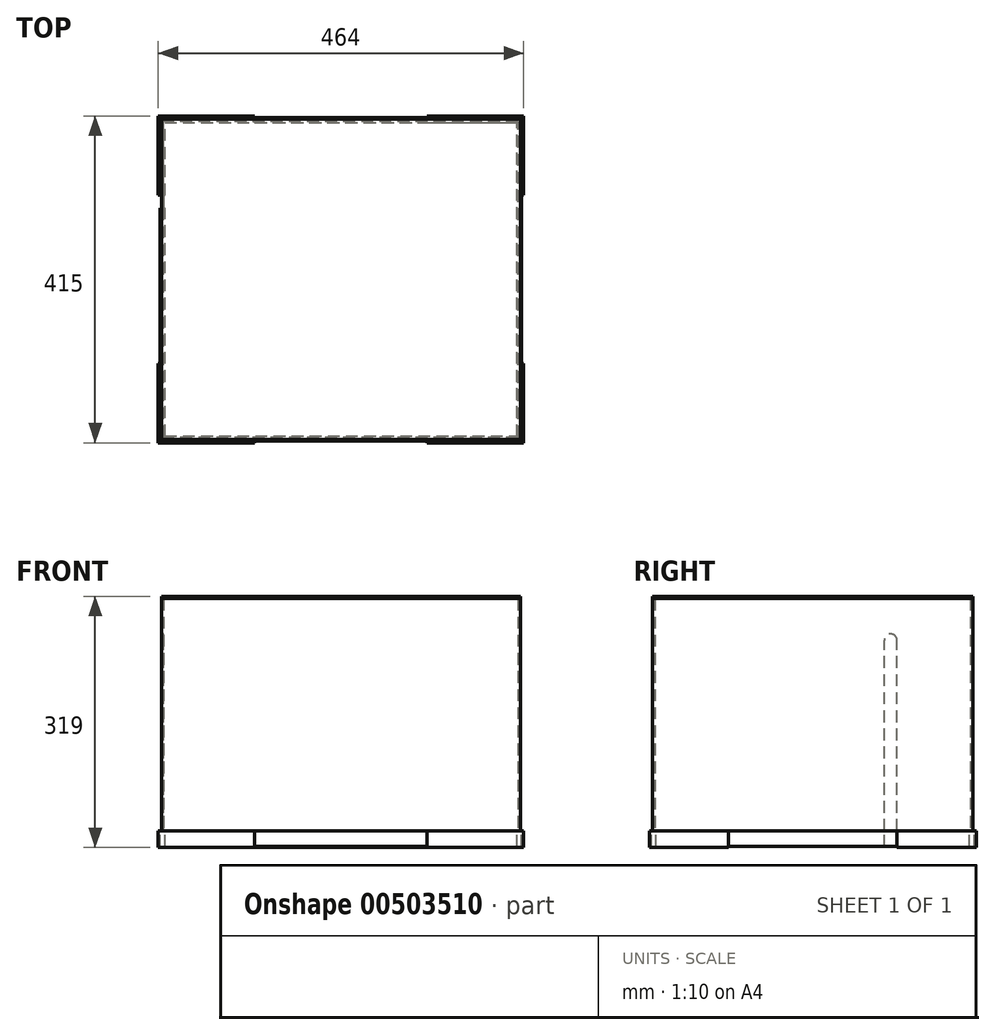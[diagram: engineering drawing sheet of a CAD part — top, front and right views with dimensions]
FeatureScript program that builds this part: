
annotation { "Feature Type Name" : "Feature", "Feature Type Description" : "" }
export const myFeature = defineFeature(function(context is Context, id is Id, definition is map)
    precondition{}
    {
        {
            var Q0;
            Q0=qCreatedBy(makeId("Right.planeOp"),FACE);
            var sketch = newSketch(context, id + "F0", { "sketchPlane" : qUnion([Q0])});
            skLineSegment(sketch, "E0.bottom", {"start": v(0, 308) * mm, "end": v(407, 308) * mm});
            skLineSegment(sketch, "E0.top", {"start": v(0, 0) * mm, "end": v(407, 0) * mm});
            skLineSegment(sketch, "E0.left", {"start": v(0, 308) * mm, "end": v(0, 0) * mm});
            skLineSegment(sketch, "E0.right", {"start": v(407, 308) * mm, "end": v(407, 0) * mm});
            skLineSegment(sketch, "E1.0", {"start": v(3, 305) * mm, "end": v(3, 0) * mm});
            skLineSegment(sketch, "E1.1", {"start": v(3, 305) * mm, "end": v(404, 305) * mm});
            skLineSegment(sketch, "E1.2", {"start": v(404, 305) * mm, "end": v(404, 0) * mm});
            skLineSegment(sketch, "E2", {"start": v(404, 305) * mm, "end": v(407, 305) * mm});
            skLineSegment(sketch, "E3", {"start": v(3, 305) * mm, "end": v(0, 305) * mm});
            skLineSegment(sketch, "E4", {"start": v(294.34, 0) * mm, "end": v(294.34, 252.03) * mm});
            skCircle(sketch, "E5", {"center": v(302.45, 252.03) * mm, "radius": 8.1 * mm});
            skLineSegment(sketch, "E6", {"start": v(310.56, 0) * mm, "end": v(310.56, 252.03) * mm});
            skSolve(sketch);
        }
        {
            var Q0;
            {var subQ0=sQuery(id+"F0.wireOp",EDGE,"E1.0");Q0=makeQuery(id+"F0.imprint","IMPRINT",FACE,{"disambiguationData":[TD([[makeQuery(id+"F0.imprint","IMPRINT",EDGE,{"derivedFrom":subQ0}),1.0]])]});}
            extrude(context, id + "F1", {"entities" : qUnion([Q0]), "depth" : 3 * mm});
        }
        {
            var Q0;
            {var subQ1=sQuery(id+"F0.wireOp",EDGE,"E0.bottom");Q0=makeQuery(id+"F0.imprint","IMPRINT",FACE,{"disambiguationData":[TD([[makeQuery(id+"F0.imprint","IMPRINT",EDGE,{"derivedFrom":subQ1}),-1.0]])]});}
            extrude(context, id + "F2", {"entities" : qUnion([Q0]), "depth" : 456 * mm});
        }
        {
            var Q0;
            {var subQ3=sQuery(id+"F0.wireOp",EDGE,"E1.0");Q0=makeQuery(id+"F0.imprint","IMPRINT",FACE,{"disambiguationData":[TD([[makeQuery(id+"F0.imprint","IMPRINT",EDGE,{"derivedFrom":subQ3}),-1.0]])]});}
            var Q1;
            {var subQ3=sQuery(id+"F0.wireOp",EDGE,"E1.2");Q1=makeQuery(id+"F0.imprint","IMPRINT",FACE,{"disambiguationData":[TD([[makeQuery(id+"F0.imprint","IMPRINT",EDGE,{"derivedFrom":subQ3}),1.0]])]});}
            extrude(context, id + "F3", {"entities" : qUnion([Q0, Q1]), "depth" : 456 * mm});
        }
        {
            var Q0;
            Q0=makeQuery(id+"F3.opExtrude","CAP_FACE",FACE,{"disambiguationData":[OSD([sQuery(id+"F0.wireOp",EDGE,"E0.top"),sQuery(id+"F0.wireOp",EDGE,"E0.left"),sQuery(id+"F0.wireOp",EDGE,"E1.0"),sQuery(id+"F0.wireOp",EDGE,"E3")])],"isStart":false});
            var sketch = newSketch(context, id + "F4", { "sketchPlane" : qUnion([Q0])});
            skLineSegment(sketch, "E7.bottom", {"start": v(3, 0) * mm, "end": v(404, 0) * mm});
            skLineSegment(sketch, "E7.top", {"start": v(3, 305) * mm, "end": v(404, 305) * mm});
            skLineSegment(sketch, "E7.left", {"start": v(3, 0) * mm, "end": v(3, 305) * mm});
            skLineSegment(sketch, "E7.right", {"start": v(404, 0) * mm, "end": v(404, 305) * mm});
            skSolve(sketch);
        }
        {
            var Q0;
            Q0=makeQuery(id+"F4.imprint","IMPRINT",FACE,{"disambiguationData":[TD([[makeQuery(id+"F4.imprint","IMPRINT",EDGE,{"derivedFrom":sQuery(id+"F4.wireOp",EDGE,"E7.bottom")}),1.0]])]});
            extrude(context, id + "F5", {"entities" : qUnion([Q0]), "oppositeDirection" : true, "depth" : 3 * mm});
        }
        {
            var Q0;
            {var subQ0=sQuery(id+"F0.wireOp",EDGE,"E0.top");Q0=makeQuery(id+"F3.opExtrude","SWEPT_FACE",FACE,{"disambiguationData":[OSD([subQ0]),TDD([makeQuery(id+"F0.imprint","IMPRINT",EDGE,{"disambiguationData":[TD([[makeQuery(id+"F0.imprint","INTERSECT",VERTEX,{"derivedFrom":[subQ0,sQuery(id+"F0.wireOp",EDGE,"E0.left")]}),-1.0]])],"derivedFrom":subQ0})])]});}
            var sketch = newSketch(context, id + "F6", { "sketchPlane" : qUnion([Q0])});
            skLineSegment(sketch, "E8.bottom", {"start": v(0, 0) * mm, "end": v(456, 0) * mm});
            skLineSegment(sketch, "E8.top", {"start": v(0, -407) * mm, "end": v(456, -407) * mm});
            skLineSegment(sketch, "E8.left", {"start": v(0, 0) * mm, "end": v(0, -407) * mm});
            skLineSegment(sketch, "E8.right", {"start": v(456, 0) * mm, "end": v(456, -407) * mm});
            skLineSegment(sketch, "E9.0", {"start": v(457.5, 1.5) * mm, "end": v(457.5, -408.5) * mm});
            skLineSegment(sketch, "E9.1", {"start": v(-1.5, 1.5) * mm, "end": v(457.5, 1.5) * mm});
            skLineSegment(sketch, "E9.2", {"start": v(-1.5, 1.5) * mm, "end": v(-1.5, -408.5) * mm});
            skLineSegment(sketch, "E9.3", {"start": v(-1.5, -408.5) * mm, "end": v(457.5, -408.5) * mm});
            skLineSegment(sketch, "E10.0", {"start": v(4.5, -4.5) * mm, "end": v(451.5, -4.5) * mm});
            skLineSegment(sketch, "E10.1", {"start": v(4.5, -4.5) * mm, "end": v(4.5, -402.5) * mm});
            skLineSegment(sketch, "E10.2", {"start": v(4.5, -402.5) * mm, "end": v(451.5, -402.5) * mm});
            skLineSegment(sketch, "E10.3", {"start": v(451.5, -4.5) * mm, "end": v(451.5, -402.5) * mm});
            skLineSegment(sketch, "E11.bottom", {"start": v(3, -3) * mm, "end": v(453, -3) * mm});
            skLineSegment(sketch, "E11.top", {"start": v(3, -404) * mm, "end": v(453, -404) * mm});
            skLineSegment(sketch, "E11.left", {"start": v(3, -3) * mm, "end": v(3, -404) * mm});
            skLineSegment(sketch, "E11.right", {"start": v(453, -3) * mm, "end": v(453, -404) * mm});
            skLineSegment(sketch, "E12", {"start": v(118.5, -408.5) * mm, "end": v(118.5, 1.5) * mm});
            skLineSegment(sketch, "E13", {"start": v(-1.5, -310.56) * mm, "end": v(457.5, -310.56) * mm});
            skLineSegment(sketch, "E14", {"start": v(337.5, -408.5) * mm, "end": v(337.5, 1.5) * mm});
            skLineSegment(sketch, "E15", {"start": v(-1.5, -96.44) * mm, "end": v(457.5, -96.44) * mm});
            skLineSegment(sketch, "E16", {"start": v(118.5, -408.5) * mm, "end": v(118.5, -310.56) * mm, "construction": true});
            skLineSegment(sketch, "E17", {"start": v(118.5, 1.5) * mm, "end": v(118.5, -96.44) * mm, "construction": true});
            skLineSegment(sketch, "E18", {"start": v(228, 1.5) * mm, "end": v(228, -408.5) * mm});
            skLineSegment(sketch, "E19", {"start": v(-1.5, -203.5) * mm, "end": v(457.5, -203.5) * mm});
            skLineSegment(sketch, "E20", {"start": v(-1.5, -294.34) * mm, "end": v(4.5, -294.34) * mm});
            skSolve(sketch);
        }
        {
            var Q0;
            {var subQ0=sQuery(id+"F6.wireOp",EDGE,"E8.left");var subQ1=sQuery(id+"F6.wireOp",EDGE,"E8.bottom");var subQ2=makeQuery(id+"F6.imprint","INTERSECT",VERTEX,{"derivedFrom":[subQ1,subQ0]});Q0=makeQuery(id+"F6.imprint","IMPRINT",FACE,{"disambiguationData":[TD([[makeQuery(id+"F6.imprint","IMPRINT",EDGE,{"disambiguationData":[TD([[subQ2,1.0]])],"derivedFrom":subQ1}),-1.0]])]});}
            var Q1;
            {var subQ5=sQuery(id+"F6.wireOp",EDGE,"E8.bottom");var subQ7=sQuery(id+"F6.wireOp",EDGE,"E8.left");var subQ9=makeQuery(id+"F6.imprint","INTERSECT",VERTEX,{"derivedFrom":[subQ5,subQ7]});Q1=makeQuery(id+"F6.imprint","IMPRINT",FACE,{"disambiguationData":[TD([[makeQuery(id+"F6.imprint","IMPRINT",EDGE,{"disambiguationData":[TD([[subQ9,1.0]])],"derivedFrom":subQ5}),1.0]])]});}
            var Q2;
            {var subQ0=sQuery(id+"F6.wireOp",EDGE,"E10.1");var subQ1=sQuery(id+"F6.wireOp",EDGE,"E10.0");var subQ2=makeQuery(id+"F6.imprint","INTERSECT",VERTEX,{"derivedFrom":[subQ1,subQ0]});Q2=makeQuery(id+"F6.imprint","IMPRINT",FACE,{"disambiguationData":[TD([[makeQuery(id+"F6.imprint","IMPRINT",EDGE,{"disambiguationData":[TD([[subQ2,-1.0]])],"derivedFrom":subQ1}),1.0]])]});}
            var Q3;
            {var subQ0=sQuery(id+"F6.wireOp",EDGE,"E8.left");var subQ3=sQuery(id+"F6.wireOp",EDGE,"E15");var subQ4=makeQuery(id+"F6.imprint","INTERSECT",VERTEX,{"derivedFrom":[subQ0,subQ3]});Q3=makeQuery(id+"F6.imprint","IMPRINT",FACE,{"disambiguationData":[TD([[makeQuery(id+"F6.imprint","IMPRINT",EDGE,{"disambiguationData":[TD([[subQ4,-1.0]])],"derivedFrom":subQ3}),1.0]])]});}
            var Q4;
            {var subQ7=sQuery(id+"F6.wireOp",EDGE,"E8.left");var subQ8=sQuery(id+"F6.wireOp",EDGE,"E8.top");var subQ9=makeQuery(id+"F6.imprint","INTERSECT",VERTEX,{"derivedFrom":[subQ8,subQ7]});Q4=makeQuery(id+"F6.imprint","IMPRINT",FACE,{"disambiguationData":[TD([[makeQuery(id+"F6.imprint","IMPRINT",EDGE,{"disambiguationData":[TD([[subQ9,-1.0]])],"derivedFrom":subQ8}),-1.0]])]});}
            var Q5;
            {var subQ7=sQuery(id+"F6.wireOp",EDGE,"E8.left");var subQ8=sQuery(id+"F6.wireOp",EDGE,"E8.top");var subQ9=makeQuery(id+"F6.imprint","INTERSECT",VERTEX,{"derivedFrom":[subQ8,subQ7]});Q5=makeQuery(id+"F6.imprint","IMPRINT",FACE,{"disambiguationData":[TD([[makeQuery(id+"F6.imprint","IMPRINT",EDGE,{"disambiguationData":[TD([[subQ9,-1.0]])],"derivedFrom":subQ8}),1.0]])]});}
            var Q6;
            {var subQ7=sQuery(id+"F6.wireOp",EDGE,"E10.2");var subQ8=sQuery(id+"F6.wireOp",EDGE,"E10.1");var subQ9=makeQuery(id+"F6.imprint","INTERSECT",VERTEX,{"derivedFrom":[subQ8,subQ7]});Q6=makeQuery(id+"F6.imprint","IMPRINT",FACE,{"disambiguationData":[TD([[makeQuery(id+"F6.imprint","IMPRINT",EDGE,{"disambiguationData":[TD([[subQ9,1.0]])],"derivedFrom":subQ8}),-1.0]])]});}
            var Q7;
            {var subQ5=sQuery(id+"F6.wireOp",EDGE,"E8.top");var subQ7=sQuery(id+"F6.wireOp",EDGE,"E8.right");var subQ8=makeQuery(id+"F6.imprint","INTERSECT",VERTEX,{"derivedFrom":[subQ5,subQ7]});Q7=makeQuery(id+"F6.imprint","IMPRINT",FACE,{"disambiguationData":[TD([[makeQuery(id+"F6.imprint","IMPRINT",EDGE,{"disambiguationData":[TD([[subQ8,1.0]])],"derivedFrom":subQ5}),-1.0]])]});}
            var Q8;
            {var subQ6=sQuery(id+"F6.wireOp",EDGE,"E8.top");var subQ9=sQuery(id+"F6.wireOp",EDGE,"E8.right");var subQ10=makeQuery(id+"F6.imprint","INTERSECT",VERTEX,{"derivedFrom":[subQ6,subQ9]});Q8=makeQuery(id+"F6.imprint","IMPRINT",FACE,{"disambiguationData":[TD([[makeQuery(id+"F6.imprint","IMPRINT",EDGE,{"disambiguationData":[TD([[subQ10,1.0]])],"derivedFrom":subQ6}),1.0]])]});}
            var Q9;
            {var subQ7=sQuery(id+"F6.wireOp",EDGE,"E10.3");var subQ8=sQuery(id+"F6.wireOp",EDGE,"E10.2");var subQ9=makeQuery(id+"F6.imprint","INTERSECT",VERTEX,{"derivedFrom":[subQ8,subQ7]});Q9=makeQuery(id+"F6.imprint","IMPRINT",FACE,{"disambiguationData":[TD([[makeQuery(id+"F6.imprint","IMPRINT",EDGE,{"disambiguationData":[TD([[subQ9,1.0]])],"derivedFrom":subQ8}),-1.0]])]});}
            var Q10;
            {var subQ5=sQuery(id+"F6.wireOp",EDGE,"E8.right");var subQ8=sQuery(id+"F6.wireOp",EDGE,"E8.bottom");var subQ9=makeQuery(id+"F6.imprint","INTERSECT",VERTEX,{"derivedFrom":[subQ8,subQ5]});Q10=makeQuery(id+"F6.imprint","IMPRINT",FACE,{"disambiguationData":[TD([[makeQuery(id+"F6.imprint","IMPRINT",EDGE,{"disambiguationData":[TD([[subQ9,-1.0]])],"derivedFrom":subQ8}),-1.0]])]});}
            var Q11;
            {var subQ1=sQuery(id+"F6.wireOp",EDGE,"E8.bottom");var subQ7=sQuery(id+"F6.wireOp",EDGE,"E8.right");var subQ8=makeQuery(id+"F6.imprint","INTERSECT",VERTEX,{"derivedFrom":[subQ1,subQ7]});Q11=makeQuery(id+"F6.imprint","IMPRINT",FACE,{"disambiguationData":[TD([[makeQuery(id+"F6.imprint","IMPRINT",EDGE,{"disambiguationData":[TD([[subQ8,-1.0]])],"derivedFrom":subQ1}),1.0]])]});}
            var Q12;
            {var subQ7=sQuery(id+"F6.wireOp",EDGE,"E10.0");var subQ9=sQuery(id+"F6.wireOp",EDGE,"E10.3");var subQ10=makeQuery(id+"F6.imprint","INTERSECT",VERTEX,{"derivedFrom":[subQ7,subQ9]});Q12=makeQuery(id+"F6.imprint","IMPRINT",FACE,{"disambiguationData":[TD([[makeQuery(id+"F6.imprint","IMPRINT",EDGE,{"disambiguationData":[TD([[subQ10,1.0]])],"derivedFrom":subQ7}),1.0]])]});}
            var Q13;
            {var subQ0=sQuery(id+"F6.wireOp",EDGE,"E8.right");var subQ3=sQuery(id+"F6.wireOp",EDGE,"E15");var subQ4=makeQuery(id+"F6.imprint","INTERSECT",VERTEX,{"derivedFrom":[subQ0,subQ3]});Q13=makeQuery(id+"F6.imprint","IMPRINT",FACE,{"disambiguationData":[TD([[makeQuery(id+"F6.imprint","IMPRINT",EDGE,{"disambiguationData":[TD([[subQ4,1.0]])],"derivedFrom":subQ3}),1.0]])]});}
            extrude(context, id + "F7", {"entities" : qUnion([Q0, Q1, Q2, Q3, Q4, Q5, Q6, Q7, Q8, Q9, Q10, Q11, Q12, Q13]), "depth" : 10 * mm});
        }
        {
            var Q0;
            {var subQ5=sQuery(id+"F6.wireOp",EDGE,"E8.top");var subQ7=sQuery(id+"F6.wireOp",EDGE,"E8.right");var subQ8=makeQuery(id+"F6.imprint","INTERSECT",VERTEX,{"derivedFrom":[subQ5,subQ7]});Q0=makeQuery(id+"F6.imprint","IMPRINT",FACE,{"disambiguationData":[TD([[makeQuery(id+"F6.imprint","IMPRINT",EDGE,{"disambiguationData":[TD([[subQ8,1.0]])],"derivedFrom":subQ5}),-1.0]])]});}
            var Q1;
            {var subQ7=sQuery(id+"F6.wireOp",EDGE,"E10.3");var subQ8=sQuery(id+"F6.wireOp",EDGE,"E10.2");var subQ9=makeQuery(id+"F6.imprint","INTERSECT",VERTEX,{"derivedFrom":[subQ8,subQ7]});Q1=makeQuery(id+"F6.imprint","IMPRINT",FACE,{"disambiguationData":[TD([[makeQuery(id+"F6.imprint","IMPRINT",EDGE,{"disambiguationData":[TD([[subQ9,1.0]])],"derivedFrom":subQ8}),-1.0]])]});}
            var Q2;
            {var subQ5=sQuery(id+"F6.wireOp",EDGE,"E8.right");var subQ8=sQuery(id+"F6.wireOp",EDGE,"E8.bottom");var subQ9=makeQuery(id+"F6.imprint","INTERSECT",VERTEX,{"derivedFrom":[subQ8,subQ5]});Q2=makeQuery(id+"F6.imprint","IMPRINT",FACE,{"disambiguationData":[TD([[makeQuery(id+"F6.imprint","IMPRINT",EDGE,{"disambiguationData":[TD([[subQ9,-1.0]])],"derivedFrom":subQ8}),-1.0]])]});}
            var Q3;
            {var subQ7=sQuery(id+"F6.wireOp",EDGE,"E10.0");var subQ9=sQuery(id+"F6.wireOp",EDGE,"E10.3");var subQ10=makeQuery(id+"F6.imprint","INTERSECT",VERTEX,{"derivedFrom":[subQ7,subQ9]});Q3=makeQuery(id+"F6.imprint","IMPRINT",FACE,{"disambiguationData":[TD([[makeQuery(id+"F6.imprint","IMPRINT",EDGE,{"disambiguationData":[TD([[subQ10,1.0]])],"derivedFrom":subQ7}),1.0]])]});}
            var Q4;
            {var subQ7=sQuery(id+"F6.wireOp",EDGE,"E8.left");var subQ8=sQuery(id+"F6.wireOp",EDGE,"E8.top");var subQ9=makeQuery(id+"F6.imprint","INTERSECT",VERTEX,{"derivedFrom":[subQ8,subQ7]});Q4=makeQuery(id+"F6.imprint","IMPRINT",FACE,{"disambiguationData":[TD([[makeQuery(id+"F6.imprint","IMPRINT",EDGE,{"disambiguationData":[TD([[subQ9,-1.0]])],"derivedFrom":subQ8}),-1.0]])]});}
            var Q5;
            {var subQ7=sQuery(id+"F6.wireOp",EDGE,"E10.2");var subQ8=sQuery(id+"F6.wireOp",EDGE,"E10.1");var subQ9=makeQuery(id+"F6.imprint","INTERSECT",VERTEX,{"derivedFrom":[subQ8,subQ7]});Q5=makeQuery(id+"F6.imprint","IMPRINT",FACE,{"disambiguationData":[TD([[makeQuery(id+"F6.imprint","IMPRINT",EDGE,{"disambiguationData":[TD([[subQ9,1.0]])],"derivedFrom":subQ8}),-1.0]])]});}
            var Q6;
            {var subQ0=sQuery(id+"F6.wireOp",EDGE,"E8.left");var subQ1=sQuery(id+"F6.wireOp",EDGE,"E8.bottom");var subQ2=makeQuery(id+"F6.imprint","INTERSECT",VERTEX,{"derivedFrom":[subQ1,subQ0]});Q6=makeQuery(id+"F6.imprint","IMPRINT",FACE,{"disambiguationData":[TD([[makeQuery(id+"F6.imprint","IMPRINT",EDGE,{"disambiguationData":[TD([[subQ2,1.0]])],"derivedFrom":subQ1}),-1.0]])]});}
            var Q7;
            {var subQ0=sQuery(id+"F6.wireOp",EDGE,"E10.1");var subQ1=sQuery(id+"F6.wireOp",EDGE,"E10.0");var subQ2=makeQuery(id+"F6.imprint","INTERSECT",VERTEX,{"derivedFrom":[subQ1,subQ0]});Q7=makeQuery(id+"F6.imprint","IMPRINT",FACE,{"disambiguationData":[TD([[makeQuery(id+"F6.imprint","IMPRINT",EDGE,{"disambiguationData":[TD([[subQ2,-1.0]])],"derivedFrom":subQ1}),1.0]])]});}
            extrude(context, id + "F8", {"entities" : qUnion([Q0, Q1, Q2, Q3, Q4, Q5, Q6, Q7]), "operationType" : NewBodyOperationType.ADD, "oppositeDirection" : true, "depth" : 10 * mm});
        }
        {
            var Q0;
            {var subQ0=sQuery(id+"F6.wireOp",EDGE,"E14");var subQ1=sQuery(id+"F6.wireOp",EDGE,"E8.bottom");var subQ2=makeQuery(id+"F6.imprint","INTERSECT",VERTEX,{"derivedFrom":[subQ1,subQ0]});Q0=makeQuery(id+"F6.imprint","IMPRINT",FACE,{"disambiguationData":[TD([[makeQuery(id+"F6.imprint","IMPRINT",EDGE,{"disambiguationData":[TD([[subQ2,-1.0]])],"derivedFrom":subQ1}),1.0]])]});}
            var Q1;
            {var subQ0=sQuery(id+"F6.wireOp",EDGE,"E18");var subQ1=sQuery(id+"F6.wireOp",EDGE,"E10.0");var subQ2=makeQuery(id+"F6.imprint","INTERSECT",VERTEX,{"derivedFrom":[subQ1,subQ0]});Q1=makeQuery(id+"F6.imprint","IMPRINT",FACE,{"disambiguationData":[TD([[makeQuery(id+"F6.imprint","IMPRINT",EDGE,{"disambiguationData":[TD([[subQ2,-1.0]])],"derivedFrom":subQ1}),1.0]])]});}
            var Q2;
            {var subQ0=sQuery(id+"F6.wireOp",EDGE,"E14");var subQ1=sQuery(id+"F6.wireOp",EDGE,"E8.bottom");var subQ2=makeQuery(id+"F6.imprint","INTERSECT",VERTEX,{"derivedFrom":[subQ1,subQ0]});Q2=makeQuery(id+"F6.imprint","IMPRINT",FACE,{"disambiguationData":[TD([[makeQuery(id+"F6.imprint","IMPRINT",EDGE,{"disambiguationData":[TD([[subQ2,-1.0]])],"derivedFrom":subQ1}),-1.0]])]});}
            var Q3;
            {var subQ0=sQuery(id+"F6.wireOp",EDGE,"E12");var subQ1=sQuery(id+"F6.wireOp",EDGE,"E8.top");var subQ2=makeQuery(id+"F6.imprint","INTERSECT",VERTEX,{"derivedFrom":[subQ1,subQ0]});Q3=makeQuery(id+"F6.imprint","IMPRINT",FACE,{"disambiguationData":[TD([[makeQuery(id+"F6.imprint","IMPRINT",EDGE,{"disambiguationData":[TD([[subQ2,-1.0]])],"derivedFrom":subQ1}),-1.0]])]});}
            var Q4;
            {var subQ0=sQuery(id+"F6.wireOp",EDGE,"E12");var subQ1=sQuery(id+"F6.wireOp",EDGE,"E8.top");var subQ2=makeQuery(id+"F6.imprint","INTERSECT",VERTEX,{"derivedFrom":[subQ1,subQ0]});Q4=makeQuery(id+"F6.imprint","IMPRINT",FACE,{"disambiguationData":[TD([[makeQuery(id+"F6.imprint","IMPRINT",EDGE,{"disambiguationData":[TD([[subQ2,-1.0]])],"derivedFrom":subQ1}),1.0]])]});}
            var Q5;
            {var subQ0=sQuery(id+"F6.wireOp",EDGE,"E12");var subQ1=sQuery(id+"F6.wireOp",EDGE,"E10.2");var subQ2=makeQuery(id+"F6.imprint","INTERSECT",VERTEX,{"derivedFrom":[subQ1,subQ0]});Q5=makeQuery(id+"F6.imprint","IMPRINT",FACE,{"disambiguationData":[TD([[makeQuery(id+"F6.imprint","IMPRINT",EDGE,{"disambiguationData":[TD([[subQ2,-1.0]])],"derivedFrom":subQ1}),-1.0]])]});}
            var Q6;
            {var subQ0=sQuery(id+"F6.wireOp",EDGE,"E19");var subQ1=sQuery(id+"F6.wireOp",EDGE,"E8.right");var subQ2=makeQuery(id+"F6.imprint","INTERSECT",VERTEX,{"derivedFrom":[subQ1,subQ0]});Q6=makeQuery(id+"F6.imprint","IMPRINT",FACE,{"disambiguationData":[TD([[makeQuery(id+"F6.imprint","IMPRINT",EDGE,{"disambiguationData":[TD([[subQ2,-1.0]])],"derivedFrom":subQ1}),1.0]])]});}
            var Q7;
            {var subQ0=sQuery(id+"F6.wireOp",EDGE,"E19");var subQ1=sQuery(id+"F6.wireOp",EDGE,"E8.right");var subQ2=makeQuery(id+"F6.imprint","INTERSECT",VERTEX,{"derivedFrom":[subQ1,subQ0]});Q7=makeQuery(id+"F6.imprint","IMPRINT",FACE,{"disambiguationData":[TD([[makeQuery(id+"F6.imprint","IMPRINT",EDGE,{"disambiguationData":[TD([[subQ2,-1.0]])],"derivedFrom":subQ1}),-1.0]])]});}
            var Q8;
            {var subQ0=sQuery(id+"F6.wireOp",EDGE,"E19");var subQ1=sQuery(id+"F6.wireOp",EDGE,"E10.3");var subQ2=makeQuery(id+"F6.imprint","INTERSECT",VERTEX,{"derivedFrom":[subQ1,subQ0]});Q8=makeQuery(id+"F6.imprint","IMPRINT",FACE,{"disambiguationData":[TD([[makeQuery(id+"F6.imprint","IMPRINT",EDGE,{"disambiguationData":[TD([[subQ2,-1.0]])],"derivedFrom":subQ1}),1.0]])]});}
            var Q9;
            {var subQ0=sQuery(id+"F6.wireOp",EDGE,"E15");var subQ1=sQuery(id+"F6.wireOp",EDGE,"E8.left");var subQ2=makeQuery(id+"F6.imprint","INTERSECT",VERTEX,{"derivedFrom":[subQ1,subQ0]});Q9=makeQuery(id+"F6.imprint","IMPRINT",FACE,{"disambiguationData":[TD([[makeQuery(id+"F6.imprint","IMPRINT",EDGE,{"disambiguationData":[TD([[subQ2,-1.0]])],"derivedFrom":subQ1}),-1.0]])]});}
            var Q10;
            {var subQ0=sQuery(id+"F6.wireOp",EDGE,"E15");var subQ1=sQuery(id+"F6.wireOp",EDGE,"E8.left");var subQ2=makeQuery(id+"F6.imprint","INTERSECT",VERTEX,{"derivedFrom":[subQ1,subQ0]});Q10=makeQuery(id+"F6.imprint","IMPRINT",FACE,{"disambiguationData":[TD([[makeQuery(id+"F6.imprint","IMPRINT",EDGE,{"disambiguationData":[TD([[subQ2,-1.0]])],"derivedFrom":subQ1}),1.0]])]});}
            var Q11;
            {var subQ0=sQuery(id+"F6.wireOp",EDGE,"E15");var subQ1=sQuery(id+"F6.wireOp",EDGE,"E10.1");var subQ2=makeQuery(id+"F6.imprint","INTERSECT",VERTEX,{"derivedFrom":[subQ1,subQ0]});Q11=makeQuery(id+"F6.imprint","IMPRINT",FACE,{"disambiguationData":[TD([[makeQuery(id+"F6.imprint","IMPRINT",EDGE,{"disambiguationData":[TD([[subQ2,-1.0]])],"derivedFrom":subQ1}),-1.0]])]});}
            extrude(context, id + "F9", {"entities" : qUnion([Q0, Q1, Q2, Q3, Q4, Q5, Q6, Q7, Q8, Q9, Q10, Q11]), "depth" : 10 * mm});
        }
        {
            var Q0;
            {var subQ0=sQuery(id+"F6.wireOp",EDGE,"E19");var subQ1=sQuery(id+"F6.wireOp",EDGE,"E8.right");var subQ2=makeQuery(id+"F6.imprint","INTERSECT",VERTEX,{"derivedFrom":[subQ1,subQ0]});Q0=makeQuery(id+"F6.imprint","IMPRINT",FACE,{"disambiguationData":[TD([[makeQuery(id+"F6.imprint","IMPRINT",EDGE,{"disambiguationData":[TD([[subQ2,-1.0]])],"derivedFrom":subQ1}),1.0]])]});}
            var Q1;
            {var subQ0=sQuery(id+"F6.wireOp",EDGE,"E19");var subQ1=sQuery(id+"F6.wireOp",EDGE,"E10.3");var subQ2=makeQuery(id+"F6.imprint","INTERSECT",VERTEX,{"derivedFrom":[subQ1,subQ0]});Q1=makeQuery(id+"F6.imprint","IMPRINT",FACE,{"disambiguationData":[TD([[makeQuery(id+"F6.imprint","IMPRINT",EDGE,{"disambiguationData":[TD([[subQ2,-1.0]])],"derivedFrom":subQ1}),1.0]])]});}
            var Q2;
            {var subQ0=sQuery(id+"F6.wireOp",EDGE,"E14");var subQ1=sQuery(id+"F6.wireOp",EDGE,"E8.bottom");var subQ2=makeQuery(id+"F6.imprint","INTERSECT",VERTEX,{"derivedFrom":[subQ1,subQ0]});Q2=makeQuery(id+"F6.imprint","IMPRINT",FACE,{"disambiguationData":[TD([[makeQuery(id+"F6.imprint","IMPRINT",EDGE,{"disambiguationData":[TD([[subQ2,-1.0]])],"derivedFrom":subQ1}),-1.0]])]});}
            var Q3;
            {var subQ0=sQuery(id+"F6.wireOp",EDGE,"E18");var subQ1=sQuery(id+"F6.wireOp",EDGE,"E10.0");var subQ2=makeQuery(id+"F6.imprint","INTERSECT",VERTEX,{"derivedFrom":[subQ1,subQ0]});Q3=makeQuery(id+"F6.imprint","IMPRINT",FACE,{"disambiguationData":[TD([[makeQuery(id+"F6.imprint","IMPRINT",EDGE,{"disambiguationData":[TD([[subQ2,-1.0]])],"derivedFrom":subQ1}),1.0]])]});}
            var Q4;
            {var subQ0=sQuery(id+"F6.wireOp",EDGE,"E12");var subQ1=sQuery(id+"F6.wireOp",EDGE,"E10.2");var subQ2=makeQuery(id+"F6.imprint","INTERSECT",VERTEX,{"derivedFrom":[subQ1,subQ0]});Q4=makeQuery(id+"F6.imprint","IMPRINT",FACE,{"disambiguationData":[TD([[makeQuery(id+"F6.imprint","IMPRINT",EDGE,{"disambiguationData":[TD([[subQ2,-1.0]])],"derivedFrom":subQ1}),-1.0]])]});}
            var Q5;
            {var subQ0=sQuery(id+"F6.wireOp",EDGE,"E12");var subQ1=sQuery(id+"F6.wireOp",EDGE,"E8.top");var subQ2=makeQuery(id+"F6.imprint","INTERSECT",VERTEX,{"derivedFrom":[subQ1,subQ0]});Q5=makeQuery(id+"F6.imprint","IMPRINT",FACE,{"disambiguationData":[TD([[makeQuery(id+"F6.imprint","IMPRINT",EDGE,{"disambiguationData":[TD([[subQ2,-1.0]])],"derivedFrom":subQ1}),-1.0]])]});}
            var Q6;
            {var subQ0=sQuery(id+"F6.wireOp",EDGE,"E15");var subQ1=sQuery(id+"F6.wireOp",EDGE,"E8.left");var subQ2=makeQuery(id+"F6.imprint","INTERSECT",VERTEX,{"derivedFrom":[subQ1,subQ0]});Q6=makeQuery(id+"F6.imprint","IMPRINT",FACE,{"disambiguationData":[TD([[makeQuery(id+"F6.imprint","IMPRINT",EDGE,{"disambiguationData":[TD([[subQ2,-1.0]])],"derivedFrom":subQ1}),-1.0]])]});}
            var Q7;
            {var subQ0=sQuery(id+"F6.wireOp",EDGE,"E15");var subQ1=sQuery(id+"F6.wireOp",EDGE,"E10.1");var subQ2=makeQuery(id+"F6.imprint","INTERSECT",VERTEX,{"derivedFrom":[subQ1,subQ0]});Q7=makeQuery(id+"F6.imprint","IMPRINT",FACE,{"disambiguationData":[TD([[makeQuery(id+"F6.imprint","IMPRINT",EDGE,{"disambiguationData":[TD([[subQ2,-1.0]])],"derivedFrom":subQ1}),-1.0]])]});}
            extrude(context, id + "F10", {"entities" : qUnion([Q0, Q1, Q2, Q3, Q4, Q5, Q6, Q7]), "operationType" : NewBodyOperationType.ADD, "oppositeDirection" : true, "depth" : 10 * mm});
        }
        {
            var Q0;
            {var subQ0=sQuery(id+"F6.wireOp",EDGE,"E18");var subQ1=sQuery(id+"F6.wireOp",EDGE,"E8.top");var subQ2=makeQuery(id+"F6.imprint","INTERSECT",VERTEX,{"derivedFrom":[subQ1,subQ0]});Q0=makeQuery(id+"F6.imprint","IMPRINT",FACE,{"disambiguationData":[TD([[makeQuery(id+"F6.imprint","IMPRINT",EDGE,{"disambiguationData":[TD([[subQ2,-1.0]])],"derivedFrom":subQ1}),-1.0]])]});}
            var Q1;
            {var subQ0=sQuery(id+"F6.wireOp",EDGE,"E18");var subQ1=sQuery(id+"F6.wireOp",EDGE,"E8.top");var subQ2=makeQuery(id+"F6.imprint","INTERSECT",VERTEX,{"derivedFrom":[subQ1,subQ0]});Q1=makeQuery(id+"F6.imprint","IMPRINT",FACE,{"disambiguationData":[TD([[makeQuery(id+"F6.imprint","IMPRINT",EDGE,{"disambiguationData":[TD([[subQ2,-1.0]])],"derivedFrom":subQ1}),1.0]])]});}
            var Q2;
            {var subQ0=sQuery(id+"F6.wireOp",EDGE,"E18");var subQ1=sQuery(id+"F6.wireOp",EDGE,"E10.2");var subQ2=makeQuery(id+"F6.imprint","INTERSECT",VERTEX,{"derivedFrom":[subQ1,subQ0]});Q2=makeQuery(id+"F6.imprint","IMPRINT",FACE,{"disambiguationData":[TD([[makeQuery(id+"F6.imprint","IMPRINT",EDGE,{"disambiguationData":[TD([[subQ2,-1.0]])],"derivedFrom":subQ1}),-1.0]])]});}
            var Q3;
            {var subQ0=sQuery(id+"F6.wireOp",EDGE,"E15");var subQ1=sQuery(id+"F6.wireOp",EDGE,"E8.right");var subQ2=makeQuery(id+"F6.imprint","INTERSECT",VERTEX,{"derivedFrom":[subQ1,subQ0]});Q3=makeQuery(id+"F6.imprint","IMPRINT",FACE,{"disambiguationData":[TD([[makeQuery(id+"F6.imprint","IMPRINT",EDGE,{"disambiguationData":[TD([[subQ2,-1.0]])],"derivedFrom":subQ1}),1.0]])]});}
            var Q4;
            {var subQ0=sQuery(id+"F6.wireOp",EDGE,"E15");var subQ1=sQuery(id+"F6.wireOp",EDGE,"E8.right");var subQ2=makeQuery(id+"F6.imprint","INTERSECT",VERTEX,{"derivedFrom":[subQ1,subQ0]});Q4=makeQuery(id+"F6.imprint","IMPRINT",FACE,{"disambiguationData":[TD([[makeQuery(id+"F6.imprint","IMPRINT",EDGE,{"disambiguationData":[TD([[subQ2,-1.0]])],"derivedFrom":subQ1}),-1.0]])]});}
            var Q5;
            {var subQ0=sQuery(id+"F6.wireOp",EDGE,"E15");var subQ1=sQuery(id+"F6.wireOp",EDGE,"E10.3");var subQ2=makeQuery(id+"F6.imprint","INTERSECT",VERTEX,{"derivedFrom":[subQ1,subQ0]});Q5=makeQuery(id+"F6.imprint","IMPRINT",FACE,{"disambiguationData":[TD([[makeQuery(id+"F6.imprint","IMPRINT",EDGE,{"disambiguationData":[TD([[subQ2,-1.0]])],"derivedFrom":subQ1}),1.0]])]});}
            var Q6;
            {var subQ0=sQuery(id+"F6.wireOp",EDGE,"E18");var subQ1=sQuery(id+"F6.wireOp",EDGE,"E8.bottom");var subQ2=makeQuery(id+"F6.imprint","INTERSECT",VERTEX,{"derivedFrom":[subQ1,subQ0]});Q6=makeQuery(id+"F6.imprint","IMPRINT",FACE,{"disambiguationData":[TD([[makeQuery(id+"F6.imprint","IMPRINT",EDGE,{"disambiguationData":[TD([[subQ2,-1.0]])],"derivedFrom":subQ1}),-1.0]])]});}
            var Q7;
            {var subQ0=sQuery(id+"F6.wireOp",EDGE,"E18");var subQ1=sQuery(id+"F6.wireOp",EDGE,"E8.bottom");var subQ2=makeQuery(id+"F6.imprint","INTERSECT",VERTEX,{"derivedFrom":[subQ1,subQ0]});Q7=makeQuery(id+"F6.imprint","IMPRINT",FACE,{"disambiguationData":[TD([[makeQuery(id+"F6.imprint","IMPRINT",EDGE,{"disambiguationData":[TD([[subQ2,-1.0]])],"derivedFrom":subQ1}),1.0]])]});}
            var Q8;
            {var subQ0=sQuery(id+"F6.wireOp",EDGE,"E12");var subQ1=sQuery(id+"F6.wireOp",EDGE,"E10.0");var subQ2=makeQuery(id+"F6.imprint","INTERSECT",VERTEX,{"derivedFrom":[subQ1,subQ0]});Q8=makeQuery(id+"F6.imprint","IMPRINT",FACE,{"disambiguationData":[TD([[makeQuery(id+"F6.imprint","IMPRINT",EDGE,{"disambiguationData":[TD([[subQ2,-1.0]])],"derivedFrom":subQ1}),1.0]])]});}
            var Q9;
            {var subQ0=sQuery(id+"F6.wireOp",EDGE,"E20");var subQ1=sQuery(id+"F6.wireOp",EDGE,"E10.1");var subQ2=makeQuery(id+"F6.imprint","INTERSECT",VERTEX,{"derivedFrom":[subQ1,subQ0]});Q9=makeQuery(id+"F6.imprint","IMPRINT",FACE,{"disambiguationData":[TD([[makeQuery(id+"F6.imprint","IMPRINT",EDGE,{"disambiguationData":[TD([[subQ2,1.0]])],"derivedFrom":subQ1}),-1.0]])]});}
            var Q10;
            {var subQ0=sQuery(id+"F6.wireOp",EDGE,"E19");var subQ1=sQuery(id+"F6.wireOp",EDGE,"E8.left");var subQ2=makeQuery(id+"F6.imprint","INTERSECT",VERTEX,{"derivedFrom":[subQ1,subQ0]});Q10=makeQuery(id+"F6.imprint","IMPRINT",FACE,{"disambiguationData":[TD([[makeQuery(id+"F6.imprint","IMPRINT",EDGE,{"disambiguationData":[TD([[subQ2,-1.0]])],"derivedFrom":subQ1}),1.0]])]});}
            var Q11;
            {var subQ0=sQuery(id+"F6.wireOp",EDGE,"E19");var subQ1=sQuery(id+"F6.wireOp",EDGE,"E8.left");var subQ2=makeQuery(id+"F6.imprint","INTERSECT",VERTEX,{"derivedFrom":[subQ1,subQ0]});Q11=makeQuery(id+"F6.imprint","IMPRINT",FACE,{"disambiguationData":[TD([[makeQuery(id+"F6.imprint","IMPRINT",EDGE,{"disambiguationData":[TD([[subQ2,-1.0]])],"derivedFrom":subQ1}),-1.0]])]});}
            extrude(context, id + "F11", {"entities" : qUnion([Q0, Q1, Q2, Q3, Q4, Q5, Q6, Q7, Q8, Q9, Q10, Q11]), "depth" : 10 * mm});
        }
        {
            var Q0;
            {var subQ0=sQuery(id+"F6.wireOp",EDGE,"E20");var subQ1=sQuery(id+"F6.wireOp",EDGE,"E10.1");var subQ2=makeQuery(id+"F6.imprint","INTERSECT",VERTEX,{"derivedFrom":[subQ1,subQ0]});Q0=makeQuery(id+"F6.imprint","IMPRINT",FACE,{"disambiguationData":[TD([[makeQuery(id+"F6.imprint","IMPRINT",EDGE,{"disambiguationData":[TD([[subQ2,1.0]])],"derivedFrom":subQ1}),-1.0]])]});}
            var Q1;
            {var subQ0=sQuery(id+"F6.wireOp",EDGE,"E19");var subQ1=sQuery(id+"F6.wireOp",EDGE,"E8.left");var subQ2=makeQuery(id+"F6.imprint","INTERSECT",VERTEX,{"derivedFrom":[subQ1,subQ0]});Q1=makeQuery(id+"F6.imprint","IMPRINT",FACE,{"disambiguationData":[TD([[makeQuery(id+"F6.imprint","IMPRINT",EDGE,{"disambiguationData":[TD([[subQ2,-1.0]])],"derivedFrom":subQ1}),-1.0]])]});}
            var Q2;
            {var subQ0=sQuery(id+"F6.wireOp",EDGE,"E18");var subQ1=sQuery(id+"F6.wireOp",EDGE,"E8.top");var subQ2=makeQuery(id+"F6.imprint","INTERSECT",VERTEX,{"derivedFrom":[subQ1,subQ0]});Q2=makeQuery(id+"F6.imprint","IMPRINT",FACE,{"disambiguationData":[TD([[makeQuery(id+"F6.imprint","IMPRINT",EDGE,{"disambiguationData":[TD([[subQ2,-1.0]])],"derivedFrom":subQ1}),-1.0]])]});}
            var Q3;
            {var subQ0=sQuery(id+"F6.wireOp",EDGE,"E18");var subQ1=sQuery(id+"F6.wireOp",EDGE,"E10.2");var subQ2=makeQuery(id+"F6.imprint","INTERSECT",VERTEX,{"derivedFrom":[subQ1,subQ0]});Q3=makeQuery(id+"F6.imprint","IMPRINT",FACE,{"disambiguationData":[TD([[makeQuery(id+"F6.imprint","IMPRINT",EDGE,{"disambiguationData":[TD([[subQ2,-1.0]])],"derivedFrom":subQ1}),-1.0]])]});}
            var Q4;
            {var subQ0=sQuery(id+"F6.wireOp",EDGE,"E12");var subQ1=sQuery(id+"F6.wireOp",EDGE,"E10.0");var subQ2=makeQuery(id+"F6.imprint","INTERSECT",VERTEX,{"derivedFrom":[subQ1,subQ0]});Q4=makeQuery(id+"F6.imprint","IMPRINT",FACE,{"disambiguationData":[TD([[makeQuery(id+"F6.imprint","IMPRINT",EDGE,{"disambiguationData":[TD([[subQ2,-1.0]])],"derivedFrom":subQ1}),1.0]])]});}
            var Q5;
            {var subQ0=sQuery(id+"F6.wireOp",EDGE,"E18");var subQ1=sQuery(id+"F6.wireOp",EDGE,"E8.bottom");var subQ2=makeQuery(id+"F6.imprint","INTERSECT",VERTEX,{"derivedFrom":[subQ1,subQ0]});Q5=makeQuery(id+"F6.imprint","IMPRINT",FACE,{"disambiguationData":[TD([[makeQuery(id+"F6.imprint","IMPRINT",EDGE,{"disambiguationData":[TD([[subQ2,-1.0]])],"derivedFrom":subQ1}),-1.0]])]});}
            var Q6;
            {var subQ0=sQuery(id+"F6.wireOp",EDGE,"E15");var subQ1=sQuery(id+"F6.wireOp",EDGE,"E10.3");var subQ2=makeQuery(id+"F6.imprint","INTERSECT",VERTEX,{"derivedFrom":[subQ1,subQ0]});Q6=makeQuery(id+"F6.imprint","IMPRINT",FACE,{"disambiguationData":[TD([[makeQuery(id+"F6.imprint","IMPRINT",EDGE,{"disambiguationData":[TD([[subQ2,-1.0]])],"derivedFrom":subQ1}),1.0]])]});}
            var Q7;
            {var subQ0=sQuery(id+"F6.wireOp",EDGE,"E15");var subQ1=sQuery(id+"F6.wireOp",EDGE,"E8.right");var subQ2=makeQuery(id+"F6.imprint","INTERSECT",VERTEX,{"derivedFrom":[subQ1,subQ0]});Q7=makeQuery(id+"F6.imprint","IMPRINT",FACE,{"disambiguationData":[TD([[makeQuery(id+"F6.imprint","IMPRINT",EDGE,{"disambiguationData":[TD([[subQ2,-1.0]])],"derivedFrom":subQ1}),1.0]])]});}
            extrude(context, id + "F12", {"entities" : qUnion([Q0, Q1, Q2, Q3, Q4, Q5, Q6, Q7]), "operationType" : NewBodyOperationType.ADD, "oppositeDirection" : true, "depth" : 10 * mm});
        }
        {
            var Q0;
            Q0=makeQuery(id+"F11.opExtrude","CAP_FACE",FACE,{"disambiguationData":[OSD([sQuery(id+"F6.wireOp",EDGE,"E9.3"),sQuery(id+"F6.wireOp",EDGE,"E10.2"),sQuery(id+"F6.wireOp",EDGE,"E14"),sQuery(id+"F6.wireOp",EDGE,"E18")])],"isStart":false});
            var sketch = newSketch(context, id + "F13", { "sketchPlane" : qUnion([Q0])});
            skLineSegment(sketch, "E21.bottom", {"start": v(457.5, -408.5) * mm, "end": v(-1.5, -408.5) * mm});
            skLineSegment(sketch, "E21.top", {"start": v(457.5, 1.5) * mm, "end": v(-1.5, 1.5) * mm});
            skLineSegment(sketch, "E21.left", {"start": v(457.5, -408.5) * mm, "end": v(457.5, 1.5) * mm});
            skLineSegment(sketch, "E21.right", {"start": v(-1.5, -408.5) * mm, "end": v(-1.5, 1.5) * mm});
            skLineSegment(sketch, "E22.bottom", {"start": v(451.5, -402.5) * mm, "end": v(4.5, -402.5) * mm});
            skLineSegment(sketch, "E22.top", {"start": v(451.5, -4.5) * mm, "end": v(4.5, -4.5) * mm});
            skLineSegment(sketch, "E22.left", {"start": v(451.5, -402.5) * mm, "end": v(451.5, -4.5) * mm});
            skLineSegment(sketch, "E22.right", {"start": v(4.5, -402.5) * mm, "end": v(4.5, -4.5) * mm});
            skLineSegment(sketch, "E23.0", {"start": v(458, -409) * mm, "end": v(458, 2) * mm});
            skLineSegment(sketch, "E23.1", {"start": v(458, -409) * mm, "end": v(-2, -409) * mm});
            skLineSegment(sketch, "E23.2", {"start": v(-2, -409) * mm, "end": v(-2, 2) * mm});
            skLineSegment(sketch, "E23.3", {"start": v(458, 2) * mm, "end": v(-2, 2) * mm});
            skLineSegment(sketch, "E24.0", {"start": v(460, 4) * mm, "end": v(-4, 4) * mm});
            skLineSegment(sketch, "E24.1", {"start": v(460, -411) * mm, "end": v(460, 4) * mm});
            skLineSegment(sketch, "E24.2", {"start": v(460, -411) * mm, "end": v(-4, -411) * mm});
            skLineSegment(sketch, "E24.3", {"start": v(-4, -411) * mm, "end": v(-4, 4) * mm});
            skLineSegment(sketch, "E25", {"start": v(118.5, 4) * mm, "end": v(118.5, -411) * mm});
            skLineSegment(sketch, "E26", {"start": v(-4, -96.44) * mm, "end": v(460, -96.44) * mm});
            skLineSegment(sketch, "E27", {"start": v(460, -310.56) * mm, "end": v(-4, -310.56) * mm});
            skLineSegment(sketch, "E28", {"start": v(-4, -203.5) * mm, "end": v(460, -203.5) * mm});
            skLineSegment(sketch, "E29", {"start": v(337.5, 4) * mm, "end": v(337.5, -411) * mm});
            skLineSegment(sketch, "E30", {"start": v(228, 4) * mm, "end": v(228, -411) * mm});
            skSolve(sketch);
        }
        {
            var Q0;
            {var subQ5=sQuery(id+"F13.wireOp",EDGE,"E23.3");var subQ6=sQuery(id+"F13.wireOp",EDGE,"E23.0");var subQ7=makeQuery(id+"F13.imprint","INTERSECT",VERTEX,{"derivedFrom":[subQ6,subQ5]});Q0=makeQuery(id+"F13.imprint","IMPRINT",FACE,{"disambiguationData":[TD([[makeQuery(id+"F13.imprint","IMPRINT",EDGE,{"disambiguationData":[TD([[subQ7,1.0]])],"derivedFrom":subQ6}),-1.0]])]});}
            var Q1;
            {var subQ7=sQuery(id+"F13.wireOp",EDGE,"E21.left");var subQ8=sQuery(id+"F13.wireOp",EDGE,"E21.top");var subQ9=makeQuery(id+"F13.imprint","INTERSECT",VERTEX,{"derivedFrom":[subQ8,subQ7]});Q1=makeQuery(id+"F13.imprint","IMPRINT",FACE,{"disambiguationData":[TD([[makeQuery(id+"F13.imprint","IMPRINT",EDGE,{"disambiguationData":[TD([[subQ9,-1.0]])],"derivedFrom":subQ8}),1.0]])]});}
            var Q2;
            {var subQ0=sQuery(id+"F13.wireOp",EDGE,"E22.left");var subQ1=sQuery(id+"F13.wireOp",EDGE,"E22.top");var subQ2=makeQuery(id+"F13.imprint","INTERSECT",VERTEX,{"derivedFrom":[subQ1,subQ0]});Q2=makeQuery(id+"F13.imprint","IMPRINT",FACE,{"disambiguationData":[TD([[makeQuery(id+"F13.imprint","IMPRINT",EDGE,{"disambiguationData":[TD([[subQ2,-1.0]])],"derivedFrom":subQ1}),1.0]])]});}
            var Q3;
            {var subQ5=sQuery(id+"F13.wireOp",EDGE,"E21.left");var subQ6=sQuery(id+"F13.wireOp",EDGE,"E21.top");var subQ7=makeQuery(id+"F13.imprint","INTERSECT",VERTEX,{"derivedFrom":[subQ6,subQ5]});Q3=makeQuery(id+"F13.imprint","IMPRINT",FACE,{"disambiguationData":[TD([[makeQuery(id+"F13.imprint","IMPRINT",EDGE,{"disambiguationData":[TD([[subQ7,-1.0]])],"derivedFrom":subQ6}),-1.0]])]});}
            var Q4;
            {var subQ0=sQuery(id+"F13.wireOp",EDGE,"E29");var subQ1=sQuery(id+"F13.wireOp",EDGE,"E22.bottom");var subQ2=makeQuery(id+"F13.imprint","INTERSECT",VERTEX,{"derivedFrom":[subQ1,subQ0]});var subQ3=sQuery(id+"F13.wireOp",EDGE,"E22.left");var subQ4=makeQuery(id+"F13.imprint","INTERSECT",VERTEX,{"derivedFrom":[subQ1,subQ3]});Q4=makeQuery(id+"F13.imprint","IMPRINT",FACE,{"disambiguationData":[TD([[makeQuery(id+"F13.imprint","IMPRINT",EDGE,{"disambiguationData":[TD([[subQ2,1.0],[subQ4,-1.0]])],"derivedFrom":subQ1}),-1.0]])]});}
            var Q5;
            {var subQ5=sQuery(id+"F13.wireOp",EDGE,"E29");var subQ7=sQuery(id+"F13.wireOp",EDGE,"E21.bottom");var subQ8=makeQuery(id+"F13.imprint","INTERSECT",VERTEX,{"derivedFrom":[subQ7,subQ5]});var subQ9=sQuery(id+"F13.wireOp",EDGE,"E21.left");var subQ10=makeQuery(id+"F13.imprint","INTERSECT",VERTEX,{"derivedFrom":[subQ7,subQ9]});Q5=makeQuery(id+"F13.imprint","IMPRINT",FACE,{"disambiguationData":[TD([[makeQuery(id+"F13.imprint","IMPRINT",EDGE,{"disambiguationData":[TD([[subQ8,1.0],[subQ10,-1.0]])],"derivedFrom":subQ7}),-1.0]])]});}
            var Q6;
            {var subQ5=sQuery(id+"F13.wireOp",EDGE,"E23.1");var subQ6=sQuery(id+"F13.wireOp",EDGE,"E23.0");var subQ7=makeQuery(id+"F13.imprint","INTERSECT",VERTEX,{"derivedFrom":[subQ6,subQ5]});Q6=makeQuery(id+"F13.imprint","IMPRINT",FACE,{"disambiguationData":[TD([[makeQuery(id+"F13.imprint","IMPRINT",EDGE,{"disambiguationData":[TD([[subQ7,-1.0]])],"derivedFrom":subQ6}),-1.0]])]});}
            var Q7;
            {var subQ3=sQuery(id+"F13.wireOp",EDGE,"E29");var subQ7=sQuery(id+"F13.wireOp",EDGE,"E21.left");var subQ8=sQuery(id+"F13.wireOp",EDGE,"E21.bottom");var subQ9=makeQuery(id+"F13.imprint","INTERSECT",VERTEX,{"derivedFrom":[subQ8,subQ7]});var subQ11=makeQuery(id+"F13.imprint","INTERSECT",VERTEX,{"derivedFrom":[subQ8,subQ3]});Q7=makeQuery(id+"F13.imprint","IMPRINT",FACE,{"disambiguationData":[TD([[makeQuery(id+"F13.imprint","IMPRINT",EDGE,{"disambiguationData":[TD([[subQ11,1.0],[subQ9,-1.0]])],"derivedFrom":subQ8}),1.0]])]});}
            var Q8;
            {var subQ5=sQuery(id+"F13.wireOp",EDGE,"E23.2");var subQ7=sQuery(id+"F13.wireOp",EDGE,"E23.1");var subQ8=makeQuery(id+"F13.imprint","INTERSECT",VERTEX,{"derivedFrom":[subQ7,subQ5]});Q8=makeQuery(id+"F13.imprint","IMPRINT",FACE,{"disambiguationData":[TD([[makeQuery(id+"F13.imprint","IMPRINT",EDGE,{"disambiguationData":[TD([[subQ8,1.0]])],"derivedFrom":subQ7}),1.0]])]});}
            var Q9;
            {var subQ5=sQuery(id+"F13.wireOp",EDGE,"E25");var subQ7=sQuery(id+"F13.wireOp",EDGE,"E21.bottom");var subQ8=makeQuery(id+"F13.imprint","INTERSECT",VERTEX,{"derivedFrom":[subQ7,subQ5]});var subQ9=sQuery(id+"F13.wireOp",EDGE,"E21.right");var subQ10=makeQuery(id+"F13.imprint","INTERSECT",VERTEX,{"derivedFrom":[subQ7,subQ9]});Q9=makeQuery(id+"F13.imprint","IMPRINT",FACE,{"disambiguationData":[TD([[makeQuery(id+"F13.imprint","IMPRINT",EDGE,{"disambiguationData":[TD([[subQ10,1.0],[subQ8,-1.0]])],"derivedFrom":subQ7}),1.0]])]});}
            var Q10;
            {var subQ3=sQuery(id+"F13.wireOp",EDGE,"E25");var subQ5=sQuery(id+"F13.wireOp",EDGE,"E21.right");var subQ6=sQuery(id+"F13.wireOp",EDGE,"E21.bottom");var subQ7=makeQuery(id+"F13.imprint","INTERSECT",VERTEX,{"derivedFrom":[subQ6,subQ5]});var subQ11=makeQuery(id+"F13.imprint","INTERSECT",VERTEX,{"derivedFrom":[subQ6,subQ3]});Q10=makeQuery(id+"F13.imprint","IMPRINT",FACE,{"disambiguationData":[TD([[makeQuery(id+"F13.imprint","IMPRINT",EDGE,{"disambiguationData":[TD([[subQ7,1.0],[subQ11,-1.0]])],"derivedFrom":subQ6}),-1.0]])]});}
            var Q11;
            {var subQ0=sQuery(id+"F13.wireOp",EDGE,"E22.right");var subQ1=sQuery(id+"F13.wireOp",EDGE,"E22.bottom");var subQ2=makeQuery(id+"F13.imprint","INTERSECT",VERTEX,{"derivedFrom":[subQ1,subQ0]});var subQ3=sQuery(id+"F13.wireOp",EDGE,"E25");var subQ4=makeQuery(id+"F13.imprint","INTERSECT",VERTEX,{"derivedFrom":[subQ1,subQ3]});Q11=makeQuery(id+"F13.imprint","IMPRINT",FACE,{"disambiguationData":[TD([[makeQuery(id+"F13.imprint","IMPRINT",EDGE,{"disambiguationData":[TD([[subQ2,1.0],[subQ4,-1.0]])],"derivedFrom":subQ1}),-1.0]])]});}
            var Q12;
            {var subQ5=sQuery(id+"F13.wireOp",EDGE,"E23.3");var subQ6=sQuery(id+"F13.wireOp",EDGE,"E23.2");var subQ7=makeQuery(id+"F13.imprint","INTERSECT",VERTEX,{"derivedFrom":[subQ6,subQ5]});Q12=makeQuery(id+"F13.imprint","IMPRINT",FACE,{"disambiguationData":[TD([[makeQuery(id+"F13.imprint","IMPRINT",EDGE,{"disambiguationData":[TD([[subQ7,1.0]])],"derivedFrom":subQ6}),1.0]])]});}
            var Q13;
            {var subQ6=sQuery(id+"F13.wireOp",EDGE,"E21.top");var subQ9=sQuery(id+"F13.wireOp",EDGE,"E21.right");var subQ10=makeQuery(id+"F13.imprint","INTERSECT",VERTEX,{"derivedFrom":[subQ6,subQ9]});Q13=makeQuery(id+"F13.imprint","IMPRINT",FACE,{"disambiguationData":[TD([[makeQuery(id+"F13.imprint","IMPRINT",EDGE,{"disambiguationData":[TD([[subQ10,1.0]])],"derivedFrom":subQ6}),-1.0]])]});}
            var Q14;
            {var subQ7=sQuery(id+"F13.wireOp",EDGE,"E21.right");var subQ8=sQuery(id+"F13.wireOp",EDGE,"E21.top");var subQ9=makeQuery(id+"F13.imprint","INTERSECT",VERTEX,{"derivedFrom":[subQ8,subQ7]});Q14=makeQuery(id+"F13.imprint","IMPRINT",FACE,{"disambiguationData":[TD([[makeQuery(id+"F13.imprint","IMPRINT",EDGE,{"disambiguationData":[TD([[subQ9,1.0]])],"derivedFrom":subQ8}),1.0]])]});}
            var Q15;
            {var subQ0=sQuery(id+"F13.wireOp",EDGE,"E22.right");var subQ1=sQuery(id+"F13.wireOp",EDGE,"E22.top");var subQ2=makeQuery(id+"F13.imprint","INTERSECT",VERTEX,{"derivedFrom":[subQ1,subQ0]});Q15=makeQuery(id+"F13.imprint","IMPRINT",FACE,{"disambiguationData":[TD([[makeQuery(id+"F13.imprint","IMPRINT",EDGE,{"disambiguationData":[TD([[subQ2,1.0]])],"derivedFrom":subQ1}),1.0]])]});}
            extrude(context, id + "F14", {"entities" : qUnion([Q0, Q1, Q2, Q3, Q4, Q5, Q6, Q7, Q8, Q9, Q10, Q11, Q12, Q13, Q14, Q15]), "operationType" : NewBodyOperationType.ADD, "depth" : 1 * mm});
        }
        {
            var Q0;
            {var subQ5=sQuery(id+"F13.wireOp",EDGE,"E23.3");var subQ6=sQuery(id+"F13.wireOp",EDGE,"E23.0");var subQ7=makeQuery(id+"F13.imprint","INTERSECT",VERTEX,{"derivedFrom":[subQ6,subQ5]});Q0=makeQuery(id+"F13.imprint","IMPRINT",FACE,{"disambiguationData":[TD([[makeQuery(id+"F13.imprint","IMPRINT",EDGE,{"disambiguationData":[TD([[subQ7,1.0]])],"derivedFrom":subQ6}),-1.0]])]});}
            var Q1;
            {var subQ5=sQuery(id+"F13.wireOp",EDGE,"E23.3");var subQ6=sQuery(id+"F13.wireOp",EDGE,"E23.2");var subQ7=makeQuery(id+"F13.imprint","INTERSECT",VERTEX,{"derivedFrom":[subQ6,subQ5]});Q1=makeQuery(id+"F13.imprint","IMPRINT",FACE,{"disambiguationData":[TD([[makeQuery(id+"F13.imprint","IMPRINT",EDGE,{"disambiguationData":[TD([[subQ7,1.0]])],"derivedFrom":subQ6}),1.0]])]});}
            var Q2;
            {var subQ5=sQuery(id+"F13.wireOp",EDGE,"E23.2");var subQ7=sQuery(id+"F13.wireOp",EDGE,"E23.1");var subQ8=makeQuery(id+"F13.imprint","INTERSECT",VERTEX,{"derivedFrom":[subQ7,subQ5]});Q2=makeQuery(id+"F13.imprint","IMPRINT",FACE,{"disambiguationData":[TD([[makeQuery(id+"F13.imprint","IMPRINT",EDGE,{"disambiguationData":[TD([[subQ8,1.0]])],"derivedFrom":subQ7}),1.0]])]});}
            var Q3;
            {var subQ5=sQuery(id+"F13.wireOp",EDGE,"E23.1");var subQ6=sQuery(id+"F13.wireOp",EDGE,"E23.0");var subQ7=makeQuery(id+"F13.imprint","INTERSECT",VERTEX,{"derivedFrom":[subQ6,subQ5]});Q3=makeQuery(id+"F13.imprint","IMPRINT",FACE,{"disambiguationData":[TD([[makeQuery(id+"F13.imprint","IMPRINT",EDGE,{"disambiguationData":[TD([[subQ7,-1.0]])],"derivedFrom":subQ6}),-1.0]])]});}
            extrude(context, id + "F15", {"entities" : qUnion([Q0, Q1, Q2, Q3]), "operationType" : NewBodyOperationType.ADD, "oppositeDirection" : true, "depth" : 20 * mm});
        }
    });
